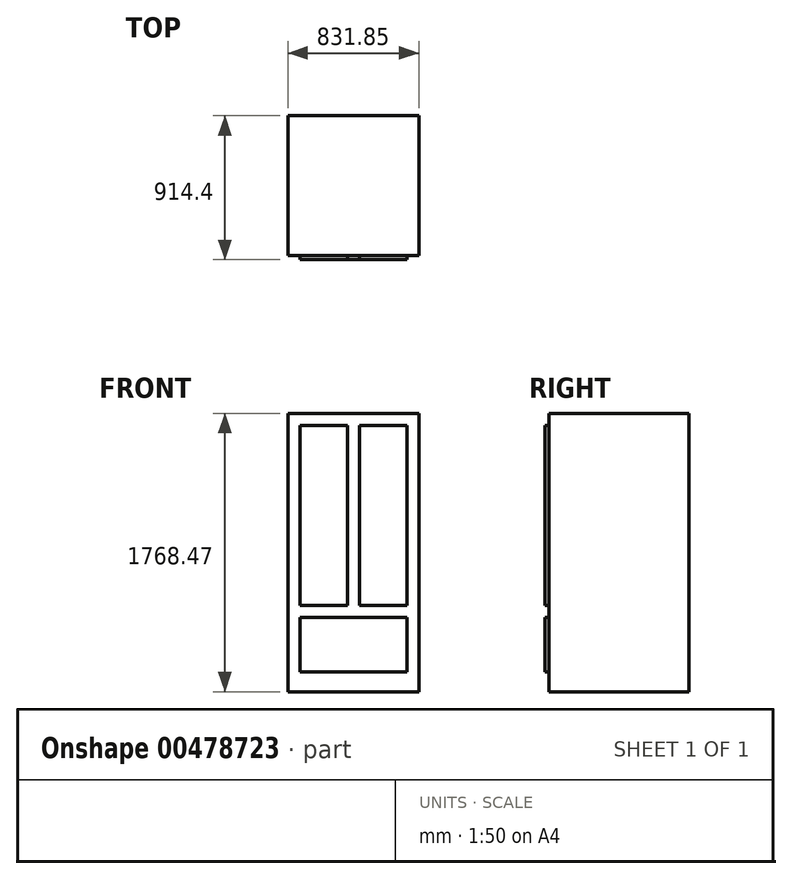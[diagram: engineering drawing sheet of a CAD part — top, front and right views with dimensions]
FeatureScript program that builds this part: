
annotation { "Feature Type Name" : "Feature", "Feature Type Description" : "" }
export const myFeature = defineFeature(function(context is Context, id is Id, definition is map)
    precondition{}
    {
        {
            var Q0;
            Q0=qCreatedBy(makeId("Top.planeOp"),FACE);
            var sketch = newSketch(context, id + "F0", { "sketchPlane" : qUnion([Q0])});
            skLineSegment(sketch, "E0.bottom", {"start": v(0, 0) * mm, "end": v(831.85, 0) * mm});
            skLineSegment(sketch, "E0.top", {"start": v(0, 889) * mm, "end": v(831.85, 889) * mm});
            skLineSegment(sketch, "E0.left", {"start": v(0, 0) * mm, "end": v(0, 889) * mm});
            skLineSegment(sketch, "E0.right", {"start": v(831.85, 0) * mm, "end": v(831.85, 889) * mm});
            skSolve(sketch);
        }
        {
            var Q0;
            Q0 = qSketchRegion(id + "F0", true);
            extrude(context, id + "F1", {"entities" : qUnion([Q0]), "depth" : 1768.47 * mm, "offsetDistance" : 25.4 * mm});
        }
        {
            var Q0;
            Q0=makeQuery(id+"F1.opExtrude","SWEPT_FACE",FACE,{"disambiguationData":[OSD([sQuery(id+"F0.wireOp",EDGE,"E0.bottom")])]});
            var sketch = newSketch(context, id + "F2", { "sketchPlane" : qUnion([Q0])});
            skLineSegment(sketch, "E1.bottom", {"start": v(76.2, 1692.28) * mm, "end": v(377.83, 1692.28) * mm});
            skLineSegment(sketch, "E1.top", {"start": v(76.2, 549.28) * mm, "end": v(377.83, 549.28) * mm});
            skLineSegment(sketch, "E1.left", {"start": v(76.2, 1692.28) * mm, "end": v(76.2, 549.27) * mm});
            skLineSegment(sketch, "E1.right", {"start": v(377.83, 1692.28) * mm, "end": v(377.83, 549.28) * mm});
            skLineSegment(sketch, "E2.bottom", {"start": v(454.03, 1692.28) * mm, "end": v(755.65, 1692.28) * mm});
            skLineSegment(sketch, "E2.top", {"start": v(454.03, 549.28) * mm, "end": v(755.65, 549.28) * mm});
            skLineSegment(sketch, "E2.left", {"start": v(454.03, 1692.28) * mm, "end": v(454.03, 549.28) * mm});
            skLineSegment(sketch, "E2.right", {"start": v(755.65, 1692.28) * mm, "end": v(755.65, 549.28) * mm});
            skLineSegment(sketch, "E3.right", {"start": v(755.65, 473.08) * mm, "end": v(755.65, 127) * mm});
            skLineSegment(sketch, "E4", {"start": v(755.65, 473.08) * mm, "end": v(76.2, 473.08) * mm});
            skLineSegment(sketch, "E5", {"start": v(76.2, 473.08) * mm, "end": v(76.2, 127) * mm});
            skLineSegment(sketch, "E6", {"start": v(76.2, 127) * mm, "end": v(755.65, 127) * mm});
            skSolve(sketch);
        }
        {
            var Q0;
            Q0 = qSketchRegion(id + "F2", true);
            extrude(context, id + "F3", {"entities" : qUnion([Q0]), "operationType" : NewBodyOperationType.ADD, "depth" : 25.4 * mm});
        }
    });
